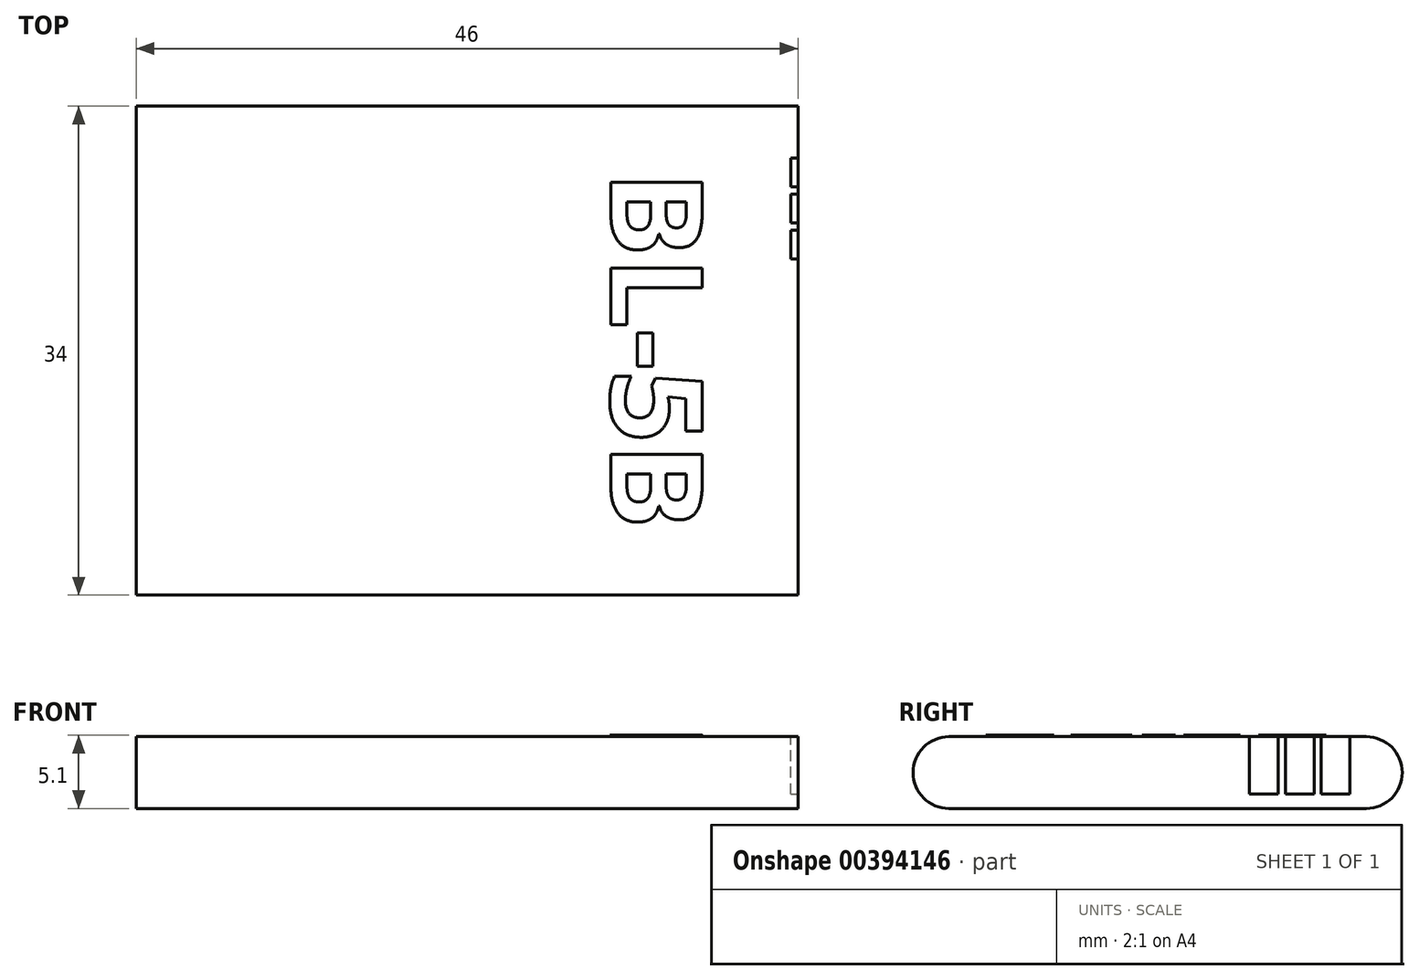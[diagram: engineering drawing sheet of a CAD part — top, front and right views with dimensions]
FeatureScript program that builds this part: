
annotation { "Feature Type Name" : "Feature", "Feature Type Description" : "" }
export const myFeature = defineFeature(function(context is Context, id is Id, definition is map)
    precondition{}
    {
        {
            var Q0;
            Q0=qCreatedBy(makeId("Top.planeOp"),FACE);
            var sketch = newSketch(context, id + "F0", { "sketchPlane" : qUnion([Q0])});
            skLineSegment(sketch, "E0.bottom", {"start": v(23, -17) * mm, "end": v(-23, -17) * mm});
            skLineSegment(sketch, "E0.top", {"start": v(23, 17) * mm, "end": v(-23, 17) * mm});
            skLineSegment(sketch, "E0.left", {"start": v(23, -17) * mm, "end": v(23, 17) * mm});
            skLineSegment(sketch, "E0.right", {"start": v(-23, -17) * mm, "end": v(-23, 17) * mm});
            skPoint(sketch, "E0.middle", {"position": v(0, 0) * mm});
            skSolve(sketch);
        }
        {
            var Q0;
            Q0=makeQuery(id+"F0.imprint","IMPRINT",FACE,{"disambiguationData":[TD([[makeQuery(id+"F0.imprint","IMPRINT",EDGE,{"derivedFrom":sQuery(id+"F0.wireOp",EDGE,"E0.bottom")}),-1.0]])]});
            extrude(context, id + "F1", {"entities" : qUnion([Q0]), "depth" : 5 * mm});
        }
        {
            var Q0;
            Q0=makeQuery(id+"F1.opExtrude","CAP_EDGE",EDGE,{"disambiguationData":[OSD([sQuery(id+"F0.wireOp",EDGE,"E0.top")])],"isStart":false});
            var Q1;
            Q1=makeQuery(id+"F1.opExtrude","CAP_EDGE",EDGE,{"disambiguationData":[OSD([sQuery(id+"F0.wireOp",EDGE,"E0.top")])],"isStart":true});
            var Q2;
            Q2=makeQuery(id+"F1.opExtrude","CAP_EDGE",EDGE,{"disambiguationData":[OSD([sQuery(id+"F0.wireOp",EDGE,"E0.bottom")])],"isStart":false});
            var Q3;
            Q3=makeQuery(id+"F1.opExtrude","CAP_EDGE",EDGE,{"disambiguationData":[OSD([sQuery(id+"F0.wireOp",EDGE,"E0.bottom")])],"isStart":true});
            fillet(context, id + "F2", {"entities" : qUnion([Q0, Q1, Q2, Q3]), "radius" : 2.5 * mm, "tangentPropagation" : true, "allowEdgeOverflow" : false});
        }
        {
            var Q0;
            Q0=makeQuery(id+"F1.opExtrude","SWEPT_FACE",FACE,{"disambiguationData":[OSD([sQuery(id+"F0.wireOp",EDGE,"E0.left")])]});
            var sketch = newSketch(context, id + "F3", { "sketchPlane" : qUnion([Q0])});
            skLineSegment(sketch, "E1.bottom", {"start": v(13.37, 1) * mm, "end": v(11.37, 1) * mm});
            skLineSegment(sketch, "E1.top", {"start": v(13.37, 5) * mm, "end": v(11.37, 5) * mm});
            skLineSegment(sketch, "E1.left", {"start": v(13.37, 1) * mm, "end": v(13.37, 5) * mm});
            skLineSegment(sketch, "E1.right", {"start": v(11.37, 1) * mm, "end": v(11.37, 5) * mm});
            skPoint(sketch, "E1.middle", {"position": v(12.37, 3) * mm});
            skLineSegment(sketch, "E2.1.0.0", {"start": v(10.87, 1) * mm, "end": v(8.87, 1) * mm});
            skLineSegment(sketch, "E2.1.0.1", {"start": v(10.87, 5) * mm, "end": v(8.87, 5) * mm});
            skLineSegment(sketch, "E2.1.0.2", {"start": v(10.87, 1) * mm, "end": v(10.87, 5) * mm});
            skLineSegment(sketch, "E2.1.0.3", {"start": v(8.87, 1) * mm, "end": v(8.87, 5) * mm});
            skPoint(sketch, "E2.1.0.4", {"position": v(9.87, 3) * mm});
            skLineSegment(sketch, "E2.2.0.0", {"start": v(8.37, 1) * mm, "end": v(6.37, 1) * mm});
            skLineSegment(sketch, "E2.2.0.1", {"start": v(8.37, 5) * mm, "end": v(6.37, 5) * mm});
            skLineSegment(sketch, "E2.2.0.2", {"start": v(8.37, 1) * mm, "end": v(8.37, 5) * mm});
            skLineSegment(sketch, "E2.2.0.3", {"start": v(6.37, 1) * mm, "end": v(6.37, 5) * mm});
            skPoint(sketch, "E2.2.0.4", {"position": v(7.37, 3) * mm});
            skLineSegment(sketch, "E2.direction1", {"start": v(11.37, 1) * mm, "end": v(8.87, 1) * mm, "construction": true});
            skSolve(sketch);
        }
        {
            var Q0;
            Q0 = qSketchRegion(id + "F3", true);
            extrude(context, id + "F4", {"entities" : qUnion([Q0]), "operationType" : NewBodyOperationType.REMOVE, "oppositeDirection" : true, "depth" : 0.5 * mm});
        }
        {
            var Q0;
            Q0=makeQuery(id+"F1.opExtrude","CAP_FACE",FACE,{"disambiguationData":[OSD([sQuery(id+"F0.wireOp",EDGE,"E0.bottom"),sQuery(id+"F0.wireOp",EDGE,"E0.top"),sQuery(id+"F0.wireOp",EDGE,"E0.left"),sQuery(id+"F0.wireOp",EDGE,"E0.right")])],"isStart":false});
            var sketch = newSketch(context, id + "F5", { "sketchPlane" : qUnion([Q0])});
            skText(sketch, "E3", { "text": "BL-5B", "fontName": "OpenSans-Bold.ttf"});
            const initialGuessF5  = {"E3": [0.01, 0.0125, 0, -1, 0.0064]};
            skSetInitialGuess(sketch, initialGuessF5);
            skSolve(sketch);
        }
        {
            var Q0;
            Q0 = qSketchRegion(id + "F5", true);
            extrude(context, id + "F6", {"entities" : qUnion([Q0]), "operationType" : NewBodyOperationType.ADD, "depth" : 0.1 * mm});
        }
    });
